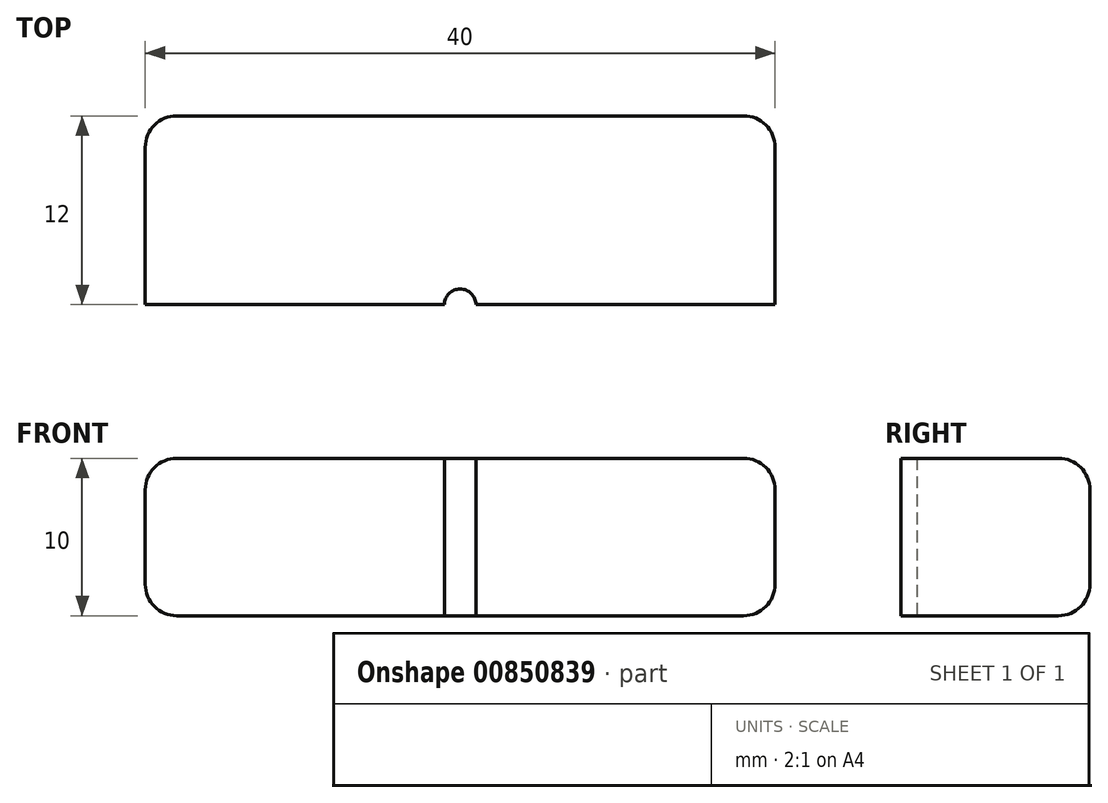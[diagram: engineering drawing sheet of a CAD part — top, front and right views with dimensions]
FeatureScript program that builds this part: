
annotation { "Feature Type Name" : "Feature", "Feature Type Description" : "" }
export const myFeature = defineFeature(function(context is Context, id is Id, definition is map)
    precondition{}
    {
        {
            var Q0;
            Q0=qCreatedBy(makeId("Top.planeOp"),FACE);
            var sketch = newSketch(context, id + "F0", { "sketchPlane" : qUnion([Q0])});
            skLineSegment(sketch, "E0.top", {"start": v(0, 17.25) * mm, "end": v(40, 17.25) * mm});
            skLineSegment(sketch, "E0.left", {"start": v(0, 5.25) * mm, "end": v(0, 17.25) * mm});
            skLineSegment(sketch, "E0.right", {"start": v(40, 0) * mm, "end": v(40, 17.25) * mm});
            skArc(sketch, "E1", {"start": v(21, 5.25) * mm, "mid": v(20, 6.25) * mm, "end": v(19, 5.25) * mm});
            skLineSegment(sketch, "E2", {"start": v(21, 5.25) * mm, "end": v(40, 5.25) * mm});
            skLineSegment(sketch, "E3", {"start": v(40, 5.25) * mm, "end": v(21, 5.25) * mm});
            skLineSegment(sketch, "E4", {"start": v(0, 5.25) * mm, "end": v(19, 5.25) * mm});
            skSolve(sketch);
        }
        {
            var Q0;
            Q0 = qSketchRegion(id + "F0", true);
            var Q1;
            {var subQ1=sQuery(id+"F0.wireOp",EDGE,"E0.top");Q1=makeQuery(id+"F0.imprint","IMPRINT",FACE,{"disambiguationData":[TD([[makeQuery(id+"F0.imprint","IMPRINT",EDGE,{"derivedFrom":subQ1}),-1.0]])]});}
            extrude(context, id + "F1", {"entities" : qUnion([Q0, Q1]), "depth" : 10 * mm, "offsetDistance" : 25 * mm});
        }
        {
            var Q0;
            Q0=makeQuery(id+"F1.opExtrude","CAP_EDGE",EDGE,{"disambiguationData":[OSD([sQuery(id+"F0.wireOp",EDGE,"E0.left")])],"isStart":true});
            var Q1;
            Q1=makeQuery(id+"F1.opExtrude","CAP_EDGE",EDGE,{"disambiguationData":[OSD([sQuery(id+"F0.wireOp",EDGE,"E0.left")])],"isStart":false});
            var Q2;
            Q2=makeQuery(id+"F1.opExtrude","SWEPT_EDGE",EDGE,{"disambiguationData":[OSD([sQuery(id+"F0.wireOp",EDGE,"E0.top"),sQuery(id+"F0.wireOp",EDGE,"E0.left")])]});
            fillet(context, id + "F2", {"entities" : qUnion([Q0, Q1, Q2]), "radius" : 2 * mm, "tangentPropagation" : true, "allowEdgeOverflow" : false});
        }
        {
            var Q0;
            Q0=makeQuery(id+"F1.opExtrude","CAP_EDGE",EDGE,{"disambiguationData":[OSD([sQuery(id+"F0.wireOp",EDGE,"E0.right")])],"isStart":true});
            var Q1;
            Q1=makeQuery(id+"F1.opExtrude","SWEPT_EDGE",EDGE,{"disambiguationData":[OSD([sQuery(id+"F0.wireOp",EDGE,"E0.top"),sQuery(id+"F0.wireOp",EDGE,"E0.right")])]});
            var Q2;
            Q2=makeQuery(id+"F1.opExtrude","CAP_EDGE",EDGE,{"disambiguationData":[OSD([sQuery(id+"F0.wireOp",EDGE,"E0.right")])],"isStart":false});
            var Q3;
            Q3=makeQuery(id+"F1.opExtrude","CAP_EDGE",EDGE,{"disambiguationData":[OSD([sQuery(id+"F0.wireOp",EDGE,"E0.top")])],"isStart":true});
            var Q4;
            Q4=makeQuery(id+"F1.opExtrude","CAP_EDGE",EDGE,{"disambiguationData":[OSD([sQuery(id+"F0.wireOp",EDGE,"E0.top")])],"isStart":false});
            fillet(context, id + "F3", {"entities" : qUnion([Q0, Q1, Q2, Q3, Q4]), "radius" : 2 * mm, "tangentPropagation" : true, "allowEdgeOverflow" : false});
        }
    });
